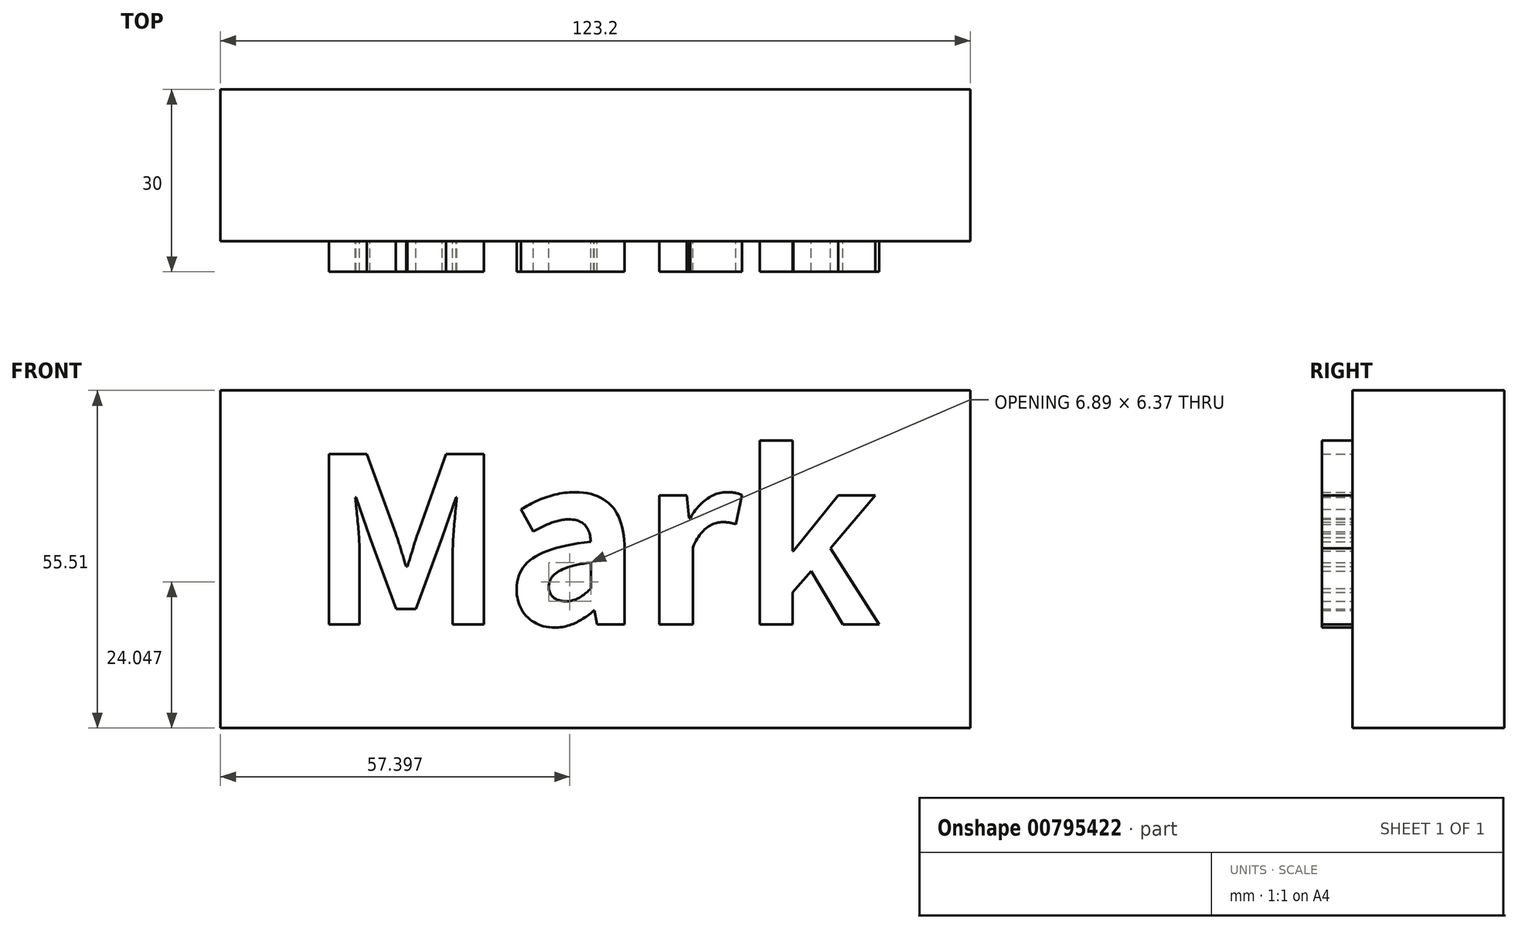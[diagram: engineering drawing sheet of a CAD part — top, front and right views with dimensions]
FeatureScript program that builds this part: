
annotation { "Feature Type Name" : "Feature", "Feature Type Description" : "" }
export const myFeature = defineFeature(function(context is Context, id is Id, definition is map)
    precondition{}
    {
        {
            var Q0;
            Q0=qCreatedBy(makeId("Front.planeOp"),FACE);
            var sketch = newSketch(context, id + "F0", { "sketchPlane" : qUnion([Q0])});
            skText(sketch, "E0", { "text": "Mark", "fontName": "NotoSansCJKkr-Bold.otf"});
            const initialGuessF0  = {"E0": [-0.0493, 0.00767, 1, 0, 0.02727]};
            skSetInitialGuess(sketch, initialGuessF0);
            skSolve(sketch);
        }
        {
            var Q0;
            Q0 = qSketchRegion(id + "F0", true);
            extrude(context, id + "F1", {"entities" : qUnion([Q0]), "depth" : 5 * mm, "offsetDistance" : 25 * mm});
        }
        {
            var Q0;
            Q0=qCreatedBy(makeId("Front.planeOp"),FACE);
            var sketch = newSketch(context, id + "F2", { "sketchPlane" : qUnion([Q0])});
            skLineSegment(sketch, "E1.bottom", {"start": v(59.53, 46.14) * mm, "end": v(-63.67, 46.14) * mm});
            skLineSegment(sketch, "E1.top", {"start": v(59.53, -9.37) * mm, "end": v(-63.67, -9.37) * mm});
            skLineSegment(sketch, "E1.left", {"start": v(59.53, 46.14) * mm, "end": v(59.53, -9.37) * mm});
            skLineSegment(sketch, "E1.right", {"start": v(-63.67, 46.14) * mm, "end": v(-63.67, -9.37) * mm});
            skSolve(sketch);
        }
        {
            var Q0;
            Q0=makeQuery(id+"F2.imprint","IMPRINT",FACE,{"disambiguationData":[TD([[makeQuery(id+"F2.imprint","IMPRINT",EDGE,{"derivedFrom":sQuery(id+"F2.wireOp",EDGE,"E1.bottom")}),1.0]])]});
            extrude(context, id + "F3", {"entities" : qUnion([Q0]), "depth" : -25 * mm, "offsetDistance" : 25 * mm});
        }
    });
